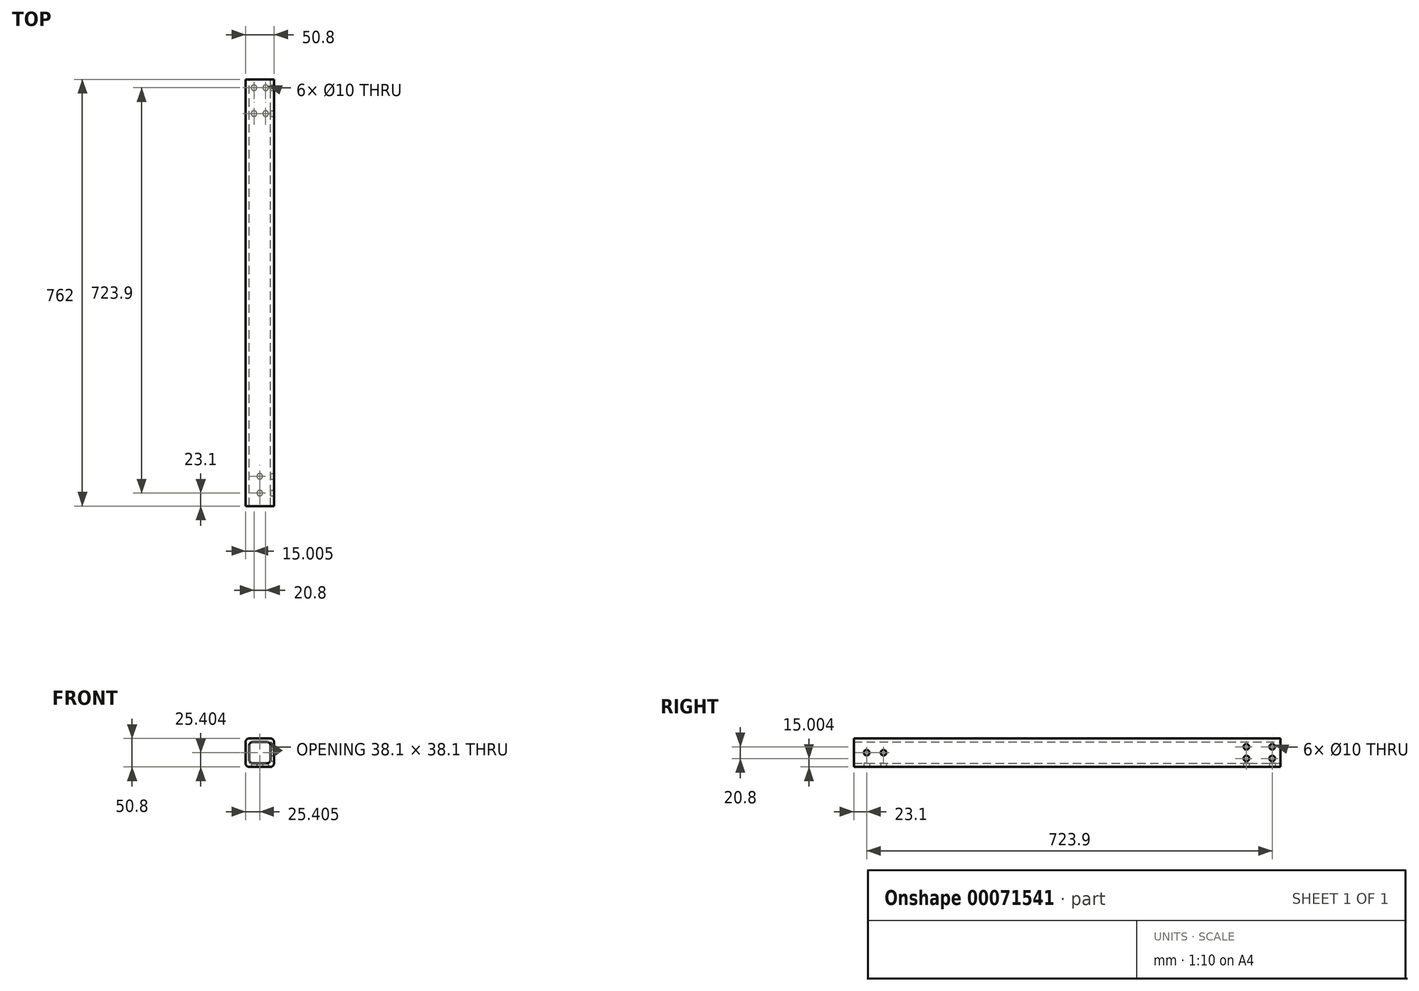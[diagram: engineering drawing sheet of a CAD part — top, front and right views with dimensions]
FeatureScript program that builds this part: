
annotation { "Feature Type Name" : "Feature", "Feature Type Description" : "" }
export const myFeature = defineFeature(function(context is Context, id is Id, definition is map)
    precondition{}
    {
        {
            var Q0;
            Q0=qCreatedBy(makeId("Front.planeOp"),FACE);
            var sketch = newSketch(context, id + "F0", { "sketchPlane" : qUnion([Q0])});
            skLineSegment(sketch, "E0.bottom", {"start": v(-17.75, 24.2) * mm, "end": v(20.35, 24.2) * mm});
            skLineSegment(sketch, "E0.top", {"start": v(-17.75, -26.6) * mm, "end": v(20.35, -26.6) * mm});
            skLineSegment(sketch, "E0.left", {"start": v(-24.1, 17.84) * mm, "end": v(-24.1, -20.26) * mm});
            skLineSegment(sketch, "E0.right", {"start": v(26.7, 17.84) * mm, "end": v(26.7, -20.26) * mm});
            skLineSegment(sketch, "E1.bottom", {"start": v(-11.4, 17.84) * mm, "end": v(14, 17.84) * mm});
            skLineSegment(sketch, "E1.top", {"start": v(-11.4, -20.26) * mm, "end": v(14, -20.26) * mm});
            skLineSegment(sketch, "E1.left", {"start": v(-17.75, 11.5) * mm, "end": v(-17.75, -13.9) * mm});
            skLineSegment(sketch, "E1.right", {"start": v(20.35, 11.5) * mm, "end": v(20.35, -13.9) * mm});
            skPoint(sketch, "E2.visualSharp", {"position": v(-17.75, 17.84) * mm});
            skArc(sketch, "E2.filletArc", {"start": v(-11.4, 17.84) * mm, "mid": v(-15.89, 15.98) * mm, "end": v(-17.75, 11.5) * mm});
            skPoint(sketch, "E3.visualSharp", {"position": v(-17.75, -20.26) * mm});
            skArc(sketch, "E3.filletArc", {"start": v(-17.75, -13.9) * mm, "mid": v(-15.89, -18.4) * mm, "end": v(-11.4, -20.26) * mm});
            skPoint(sketch, "E4.visualSharp", {"position": v(20.35, -20.26) * mm});
            skArc(sketch, "E4.filletArc", {"start": v(14, -20.26) * mm, "mid": v(18.5, -18.4) * mm, "end": v(20.35, -13.9) * mm});
            skPoint(sketch, "E5.visualSharp", {"position": v(20.35, 17.84) * mm});
            skArc(sketch, "E5.filletArc", {"start": v(20.35, 11.5) * mm, "mid": v(18.5, 15.98) * mm, "end": v(14, 17.84) * mm});
            skPoint(sketch, "E6.visualSharp", {"position": v(-24.1, 24.2) * mm});
            skArc(sketch, "E6.filletArc", {"start": v(-17.75, 24.2) * mm, "mid": v(-22.24, 22.33) * mm, "end": v(-24.1, 17.84) * mm});
            skPoint(sketch, "E7.visualSharp", {"position": v(-24.1, -26.6) * mm});
            skArc(sketch, "E7.filletArc", {"start": v(-24.1, -20.26) * mm, "mid": v(-22.24, -24.75) * mm, "end": v(-17.75, -26.6) * mm});
            skPoint(sketch, "E8.visualSharp", {"position": v(26.7, -26.6) * mm});
            skArc(sketch, "E8.filletArc", {"start": v(20.35, -26.6) * mm, "mid": v(24.84, -24.75) * mm, "end": v(26.7, -20.26) * mm});
            skPoint(sketch, "E9.visualSharp", {"position": v(26.7, 24.2) * mm});
            skArc(sketch, "E9.filletArc", {"start": v(26.7, 17.84) * mm, "mid": v(24.84, 22.33) * mm, "end": v(20.35, 24.2) * mm});
            skSolve(sketch);
        }
        {
            var Q0;
            Q0 = qSketchRegion(id + "F0", true);
            extrude(context, id + "F1", {"entities" : qUnion([Q0]), "depth" : 762 * mm});
        }
        {
            var Q0;
            Q0=makeQuery(id+"F1.opExtrude","SWEPT_FACE",FACE,{"disambiguationData":[OSD([sQuery(id+"F0.wireOp",EDGE,"E0.right")])]});
            var sketch = newSketch(context, id + "F2", { "sketchPlane" : qUnion([Q0])});
            skCircle(sketch, "E10", {"center": v(-15, 9.2) * mm, "radius": 5 * mm});
            skCircle(sketch, "E11", {"center": v(-15, -11.6) * mm, "radius": 5 * mm});
            skCircle(sketch, "E12", {"center": v(-61.2, 9.2) * mm, "radius": 5 * mm});
            skCircle(sketch, "E13", {"center": v(-61.2, -11.6) * mm, "radius": 5 * mm});
            skSolve(sketch);
        }
        {
            var Q0;
            Q0 = qSketchRegion(id + "F2", true);
            extrude(context, id + "F3", {"entities" : qUnion([Q0]), "operationType" : NewBodyOperationType.REMOVE, "oppositeDirection" : true, "depth" : 25 * mm});
        }
        {
            var Q0;
            Q0=makeQuery(id+"F1.opExtrude","SWEPT_FACE",FACE,{"disambiguationData":[OSD([sQuery(id+"F0.wireOp",EDGE,"E0.top")])]});
            var sketch = newSketch(context, id + "F4", { "sketchPlane" : qUnion([Q0])});
            skCircle(sketch, "E14", {"center": v(11.7, 15) * mm, "radius": 5 * mm});
            skCircle(sketch, "E15", {"center": v(-9.1, 15) * mm, "radius": 5 * mm});
            skCircle(sketch, "E16", {"center": v(11.7, 61.2) * mm, "radius": 5 * mm});
            skCircle(sketch, "E17", {"center": v(-9.1, 61.2) * mm, "radius": 5 * mm});
            skSolve(sketch);
        }
        {
            var Q0;
            Q0 = qSketchRegion(id + "F4", true);
            extrude(context, id + "F5", {"entities" : qUnion([Q0]), "operationType" : NewBodyOperationType.REMOVE, "oppositeDirection" : true, "depth" : 25 * mm});
        }
        {
            var Q0;
            Q0=makeQuery(id+"F1.opExtrude","SWEPT_FACE",FACE,{"disambiguationData":[OSD([sQuery(id+"F0.wireOp",EDGE,"E0.top")])]});
            var sketch = newSketch(context, id + "F6", { "sketchPlane" : qUnion([Q0])});
            skCircle(sketch, "E18", {"center": v(1.3, 738.9) * mm, "radius": 5 * mm});
            skCircle(sketch, "E19", {"center": v(1.3, 708.9) * mm, "radius": 5 * mm});
            skSolve(sketch);
        }
        {
            var Q0;
            Q0 = qSketchRegion(id + "F6", true);
            extrude(context, id + "F7", {"entities" : qUnion([Q0]), "operationType" : NewBodyOperationType.REMOVE, "oppositeDirection" : true, "depth" : 25 * mm});
        }
        {
            var Q0;
            Q0=makeQuery(id+"F1.opExtrude","SWEPT_FACE",FACE,{"disambiguationData":[OSD([sQuery(id+"F0.wireOp",EDGE,"E0.right")])]});
            var sketch = newSketch(context, id + "F8", { "sketchPlane" : qUnion([Q0])});
            skCircle(sketch, "E20", {"center": v(-738.9, -1.2) * mm, "radius": 5 * mm});
            skCircle(sketch, "E21", {"center": v(-708.9, -1.2) * mm, "radius": 5 * mm});
            skSolve(sketch);
        }
        {
            var Q0;
            Q0 = qSketchRegion(id + "F8", true);
            extrude(context, id + "F9", {"entities" : qUnion([Q0]), "operationType" : NewBodyOperationType.REMOVE, "oppositeDirection" : true, "depth" : 25 * mm});
        }
    });
